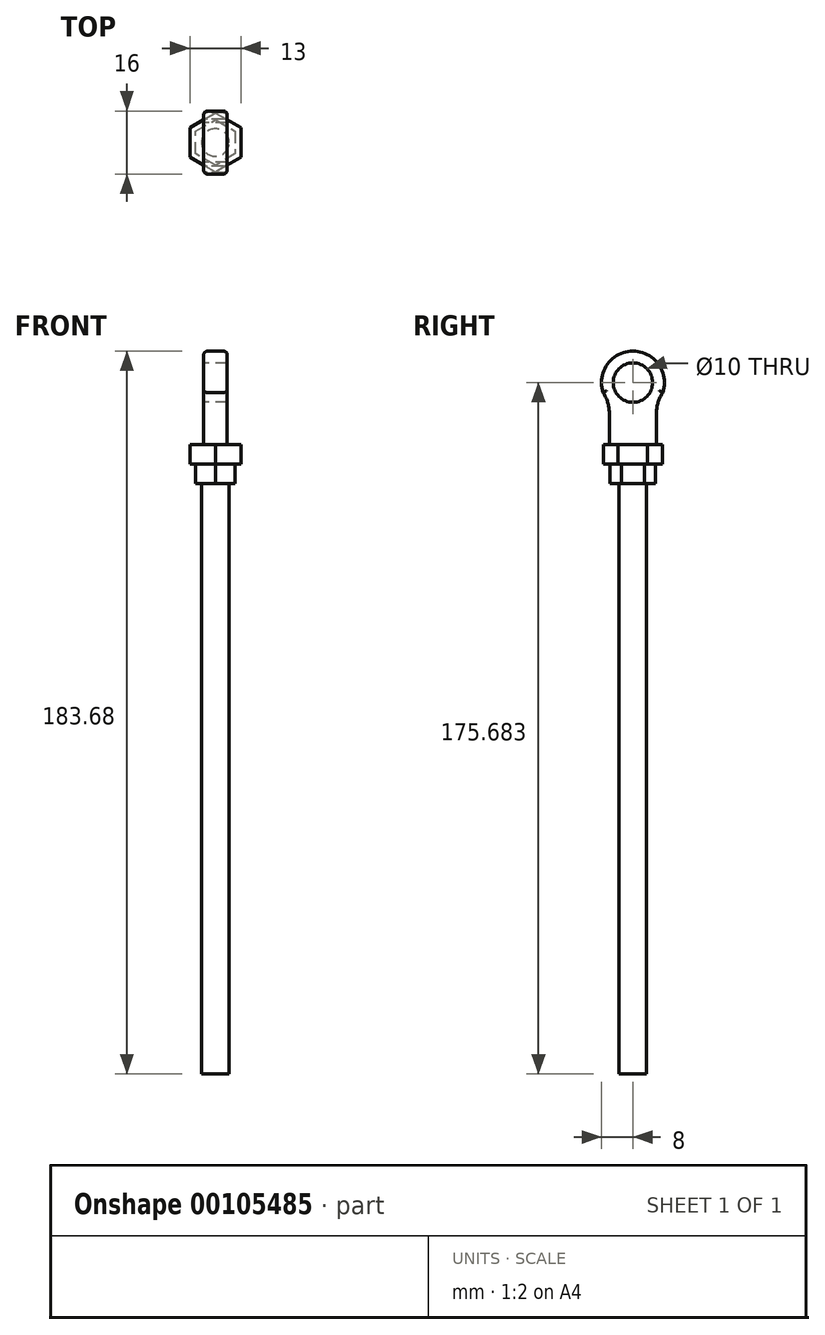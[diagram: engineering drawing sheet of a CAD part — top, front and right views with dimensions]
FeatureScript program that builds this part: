
annotation { "Feature Type Name" : "Feature", "Feature Type Description" : "" }
export const myFeature = defineFeature(function(context is Context, id is Id, definition is map)
    precondition{}
    {
        {
            var Q0;
            Q0=qCreatedBy(makeId("Top.planeOp"),FACE);
            var sketch = newSketch(context, id + "F0", { "sketchPlane" : qUnion([Q0])});
            skCircle(sketch, "E0", {"center": v(0, 0) * mm, "radius": 3.5 * mm});
            skSolve(sketch);
        }
        {
            var Q0;
            Q0=makeQuery(id+"F0.imprint","IMPRINT",FACE,{"disambiguationData":[TD([[makeQuery(id+"F0.imprint","IMPRINT",EDGE,{"derivedFrom":sQuery(id+"F0.wireOp",EDGE,"E0")}),1.0]])]});
            extrude(context, id + "F1", {"entities" : qUnion([Q0]), "depth" : 150 * mm});
        }
        {
            var Q0;
            Q0=makeQuery(id+"F1.opExtrude","CAP_FACE",FACE,{"disambiguationData":[OSD([sQuery(id+"F0.wireOp",EDGE,"E0")])],"isStart":false});
            var sketch = newSketch(context, id + "F2", { "sketchPlane" : qUnion([Q0])});
            skCircle(sketch, "E1.cCircle", {"center": v(0, 0) * mm, "radius": 5 * mm, "construction": true});
            skLineSegment(sketch, "E1.0", {"start": v(5, 2.89) * mm, "end": v(5, -2.89) * mm});
            skLineSegment(sketch, "E1.1", {"start": v(5, -2.89) * mm, "end": v(0, -5.77) * mm});
            skLineSegment(sketch, "E1.2", {"start": v(0, -5.77) * mm, "end": v(-5, -2.89) * mm});
            skLineSegment(sketch, "E1.3", {"start": v(-5, -2.89) * mm, "end": v(-5, 2.89) * mm});
            skLineSegment(sketch, "E1.4", {"start": v(-5, 2.89) * mm, "end": v(0, 5.77) * mm});
            skLineSegment(sketch, "E1.5", {"start": v(0, 5.77) * mm, "end": v(5, 2.89) * mm});
            skPoint(sketch, "E1.0.midPoint", {"position": v(5, 0) * mm});
            skSolve(sketch);
        }
        {
            var Q0;
            Q0=qSketchRegion(id+"F2",true);
            extrude(context, id + "F3", {"entities" : qUnion([Q0]), "operationType" : NewBodyOperationType.ADD, "depth" : 5 * mm});
        }
        {
            var Q0;
            Q0=makeQuery(id+"F3.opExtrude","CAP_FACE",FACE,{"disambiguationData":[OSD([sQuery(id+"F2.wireOp",EDGE,"E1.0"),sQuery(id+"F2.wireOp",EDGE,"E1.1"),sQuery(id+"F2.wireOp",EDGE,"E1.2"),sQuery(id+"F2.wireOp",EDGE,"E1.3"),sQuery(id+"F2.wireOp",EDGE,"E1.4"),sQuery(id+"F2.wireOp",EDGE,"E1.5")])],"isStart":false});
            var sketch = newSketch(context, id + "F4", { "sketchPlane" : qUnion([Q0])});
            skCircle(sketch, "E2.cCircle", {"center": v(0, 0) * mm, "radius": 6.5 * mm, "construction": true});
            skLineSegment(sketch, "E2.0", {"start": v(6.5, 3.75) * mm, "end": v(6.5, -3.75) * mm});
            skLineSegment(sketch, "E2.1", {"start": v(6.5, -3.75) * mm, "end": v(0, -7.5) * mm});
            skLineSegment(sketch, "E2.2", {"start": v(0, -7.5) * mm, "end": v(-6.5, -3.75) * mm});
            skLineSegment(sketch, "E2.3", {"start": v(-6.5, -3.75) * mm, "end": v(-6.5, 3.75) * mm});
            skLineSegment(sketch, "E2.4", {"start": v(-6.5, 3.75) * mm, "end": v(0, 7.5) * mm});
            skLineSegment(sketch, "E2.5", {"start": v(0, 7.5) * mm, "end": v(6.5, 3.75) * mm});
            skPoint(sketch, "E2.0.midPoint", {"position": v(6.5, 0) * mm});
            skSolve(sketch);
        }
        {
            var Q0;
            Q0=qSketchRegion(id+"F4",true);
            extrude(context, id + "F5", {"entities" : qUnion([Q0]), "operationType" : NewBodyOperationType.ADD, "depth" : 5 * mm});
        }
        {
            var Q0;
            Q0=qCreatedBy(makeId("Right.planeOp"),FACE);
            var sketch = newSketch(context, id + "F6", { "sketchPlane" : qUnion([Q0])});
            skLineSegment(sketch, "E3", {"start": v(0, 0) * mm, "end": v(0, 160) * mm});
            skArc(sketch, "E4", {"start": v(7.6, 173.18) * mm, "mid": v(0, 183.68) * mm, "end": v(-7.6, 173.18) * mm});
            skCircle(sketch, "E5", {"center": v(0, 175.68) * mm, "radius": 5 * mm});
            skLineSegment(sketch, "E6", {"start": v(0, 160) * mm, "end": v(-6, 160) * mm});
            skLineSegment(sketch, "E7", {"start": v(-6, 160) * mm, "end": v(-6, 168) * mm});
            skArc(sketch, "E8", {"start": v(-6, 168) * mm, "mid": v(-6.4, 170.7) * mm, "end": v(-7.6, 173.18) * mm});
            skArc(sketch, "E9.MirrorCS", {"start": v(6, 168) * mm, "mid": v(6.4, 170.7) * mm, "end": v(7.6, 173.18) * mm});
            skLineSegment(sketch, "E10.MirrorCS", {"start": v(6, 160) * mm, "end": v(6, 168) * mm});
            skLineSegment(sketch, "E11.MirrorCS", {"start": v(0, 160) * mm, "end": v(6, 160) * mm});
            skSolve(sketch);
        }
        {
            var Q0;
            Q0=qSketchRegion(id+"F6",true);
            extrude(context, id + "F7", {"entities" : qUnion([Q0]), "operationType" : NewBodyOperationType.ADD, "endBound" : BoundingType.SYMMETRIC, "depth" : 6 * mm});
        }
        {
            var Q0;
            Q0=makeQuery(id+"F7.opExtrude","CAP_EDGE",EDGE,{"disambiguationData":[OSD([sQuery(id+"F6.wireOp",EDGE,"E8")])],"isStart":false});
            var Q1;
            Q1=makeQuery(id+"F7.opExtrude","CAP_EDGE",EDGE,{"disambiguationData":[OSD([sQuery(id+"F6.wireOp",EDGE,"E4")])],"isStart":false});
            var Q2;
            Q2=makeQuery(id+"F7.opExtrude","CAP_EDGE",EDGE,{"disambiguationData":[OSD([sQuery(id+"F6.wireOp",EDGE,"E9.MirrorCS")])],"isStart":false});
            var Q3;
            Q3=makeQuery(id+"F7.opExtrude","CAP_EDGE",EDGE,{"disambiguationData":[OSD([sQuery(id+"F6.wireOp",EDGE,"E9.MirrorCS")])],"isStart":true});
            var Q4;
            Q4=makeQuery(id+"F7.opExtrude","CAP_EDGE",EDGE,{"disambiguationData":[OSD([sQuery(id+"F6.wireOp",EDGE,"E8")])],"isStart":true});
            var Q5;
            Q5=makeQuery(id+"F7.opExtrude","CAP_EDGE",EDGE,{"disambiguationData":[OSD([sQuery(id+"F6.wireOp",EDGE,"E4")])],"isStart":true});
            fillet(context, id + "F8", {"entities" : qUnion([Q0, Q1, Q2, Q3, Q4, Q5]), "radius" : 1 * mm, "tangentPropagation" : true, "allowEdgeOverflow" : false});
        }
    });
